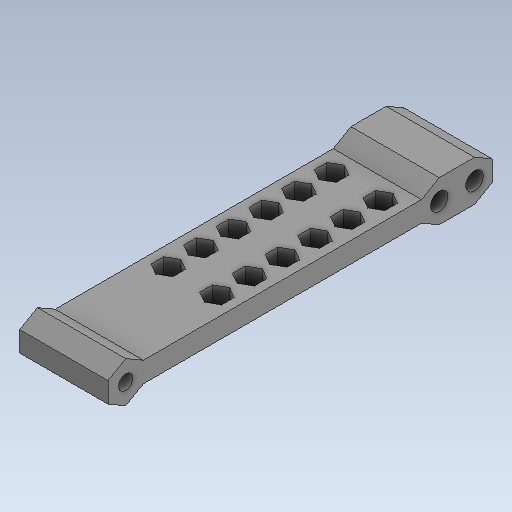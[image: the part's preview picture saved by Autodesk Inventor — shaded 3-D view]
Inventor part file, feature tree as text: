
AUTODESK INVENTOR PART (.ipt)
format: ipt  version: 2020 (Build 240168000, 168)  size: 387,072 bytes
history: native  units: in
note: dims shown in document units (in); Inventor stores cm internally (conversion verified against a paired STEP export)
features: sketch x6, extrude x5, projected_geometry x3, plane x2, mirror x1
ambient origin geometry x8: Origin, YZ Plane, XZ Plane, XY Plane, X Axis, Y Axis, Z Axis, Center Point
bodies: Solid1 (feature_tree)
feature tree (17):
  extrude  "Extrusion1"  Depth=3.4256in
  plane  "Work Plane1"
  extrude  "Extrusion2"  Depth=0.7874in
  sketch  "Sketch4"  dims[d4=0.0in d5=0.0827in]
  extrude  "Extrusion4"  Depth=0.0827in
  plane  "Work Plane2"
  extrude  "Extrusion6"  Depth=3.1106in
  mirror  "Mirror2"
  extrude  "Extrusion7"  Depth=0.315in
  sketch  "Sketch1"  dims[d0=0.1818in d1=3.4256in]
  sketch  "Sketch2"  dims[d2=0.1299in d3=0.7874in]
  sketch  "Sketch5"  dims[d6=0.7874in d7=0.0in d28=3.1106in]
  sketch  "Sketch7"  dims[d29=0.315in d31=0.315in]
  projected_geometry  "Projected Loop7"
  projected_geometry  "Projected Loop8"
  sketch  "Sketch8"  dims[d33=0.1575in d34=0.2362in d35=0.0in d38=0.315in d39=0.2756in d40=-0.3092in d41=0.0787in d42=0.0787in d43=0.0787in d44=2.3622in d46=0.2913in d47=0.3937in d49=0.3937in d51=2.3622in d53=0.2913in d54=0.3937in d56=0.3937in d58=0.0in d59=0.0in]
  projected_geometry  "Projected Loop9"
